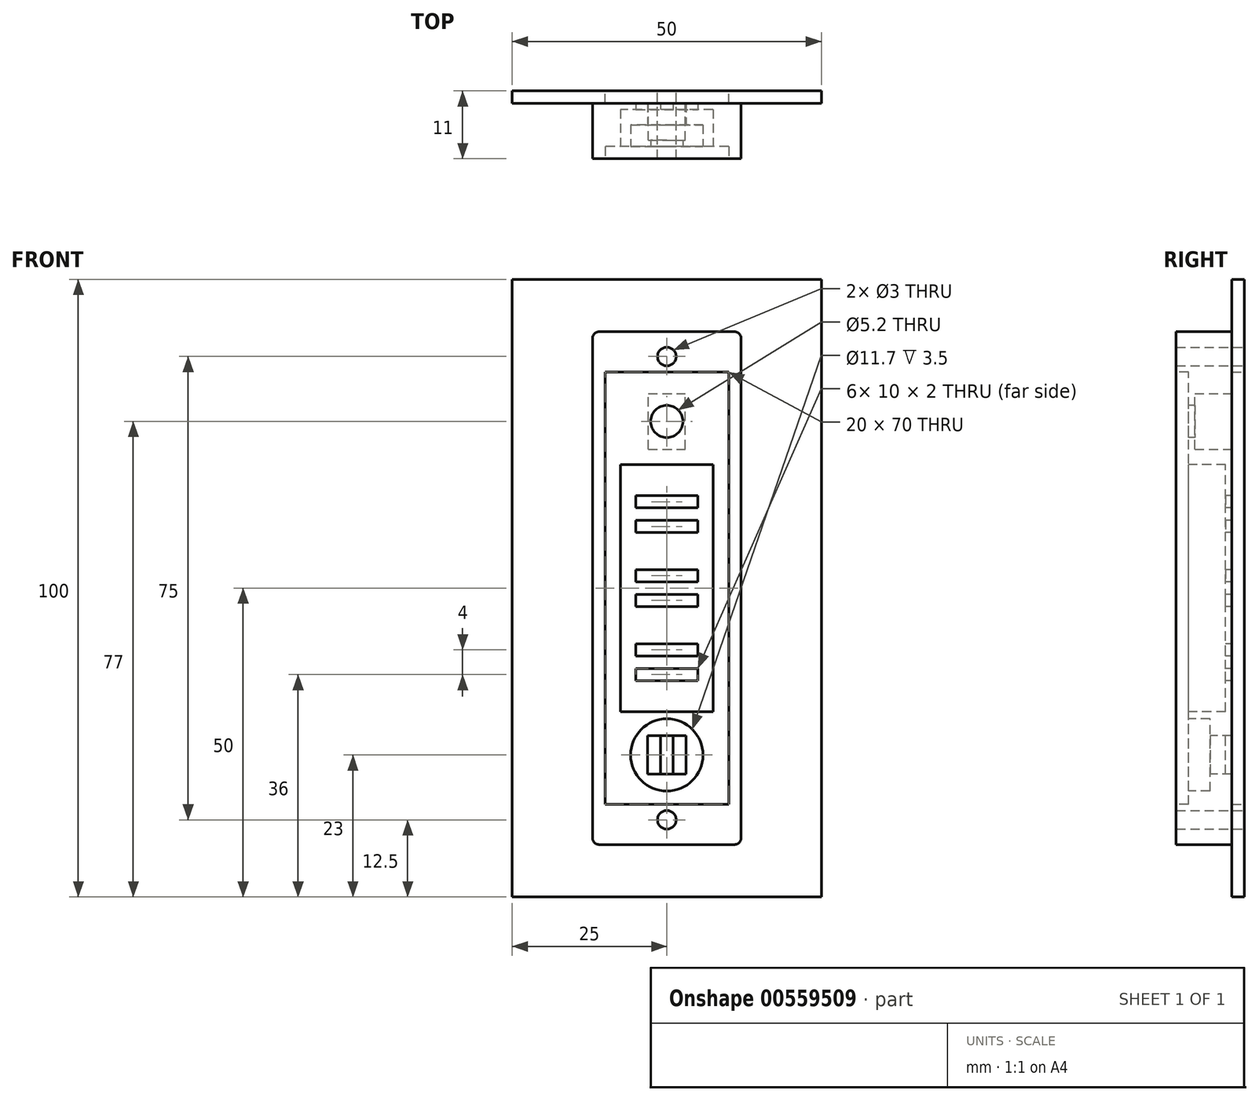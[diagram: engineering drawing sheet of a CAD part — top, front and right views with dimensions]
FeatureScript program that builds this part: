
annotation { "Feature Type Name" : "Feature", "Feature Type Description" : "" }
export const myFeature = defineFeature(function(context is Context, id is Id, definition is map)
    precondition{}
    {
        {
            var Q0;
            Q0=qCreatedBy(makeId("Front.planeOp"),FACE);
            var sketch = newSketch(context, id + "F0", { "sketchPlane" : qUnion([Q0])});
            skLineSegment(sketch, "E0.bottom", {"start": v(25, -50) * mm, "end": v(-25, -50) * mm});
            skLineSegment(sketch, "E0.top", {"start": v(25, 50) * mm, "end": v(-25, 50) * mm});
            skLineSegment(sketch, "E0.left", {"start": v(25, -50) * mm, "end": v(25, 50) * mm});
            skLineSegment(sketch, "E0.right", {"start": v(-25, -50) * mm, "end": v(-25, 50) * mm});
            skPoint(sketch, "E0.middle", {"position": v(0, 0) * mm});
            skLineSegment(sketch, "E1.bottom", {"start": v(10, -35) * mm, "end": v(-10, -35) * mm});
            skLineSegment(sketch, "E1.top", {"start": v(10, 35) * mm, "end": v(-10, 35) * mm});
            skLineSegment(sketch, "E1.left", {"start": v(10, -35) * mm, "end": v(10, 35) * mm});
            skLineSegment(sketch, "E1.right", {"start": v(-10, -35) * mm, "end": v(-10, 35) * mm});
            skCircle(sketch, "E2", {"center": v(0, 37.5) * mm, "radius": 1.5 * mm});
            skCircle(sketch, "E3", {"center": v(0, -37.5) * mm, "radius": 1.5 * mm});
            skSolve(sketch);
        }
        {
            var Q0;
            Q0=qSketchRegion(id+"F0",true);
            extrude(context, id + "F1", {"entities" : qUnion([Q0]), "depth" : 2 * mm});
        }
        {
            var Q0;
            Q0=makeQuery(id+"F1.opExtrude","CAP_FACE",FACE,{"disambiguationData":[OSD([sQuery(id+"F0.wireOp",EDGE,"E0.bottom"),sQuery(id+"F0.wireOp",EDGE,"E0.top"),sQuery(id+"F0.wireOp",EDGE,"E0.left"),sQuery(id+"F0.wireOp",EDGE,"E0.right"),sQuery(id+"F0.wireOp",EDGE,"E1.bottom"),sQuery(id+"F0.wireOp",EDGE,"E1.top"),sQuery(id+"F0.wireOp",EDGE,"E1.left"),sQuery(id+"F0.wireOp",EDGE,"E1.right"),sQuery(id+"F0.wireOp",EDGE,"E2"),sQuery(id+"F0.wireOp",EDGE,"E3")])],"isStart":false});
            var sketch = newSketch(context, id + "F2", { "sketchPlane" : qUnion([Q0])});
            skLineSegment(sketch, "E4.bottom", {"start": v(12, -41.5) * mm, "end": v(-12, -41.5) * mm});
            skLineSegment(sketch, "E4.top", {"start": v(12, 41.5) * mm, "end": v(-12, 41.5) * mm});
            skLineSegment(sketch, "E4.left", {"start": v(12, -41.5) * mm, "end": v(12, 41.5) * mm});
            skLineSegment(sketch, "E4.right", {"start": v(-12, -41.5) * mm, "end": v(-12, 41.5) * mm});
            skPoint(sketch, "E4.middle", {"position": v(0, 0) * mm});
            skCircle(sketch, "E5", {"center": v(0, 37.5) * mm, "radius": 1.5 * mm});
            skCircle(sketch, "E6", {"center": v(0, -37.5) * mm, "radius": 1.5 * mm});
            skSolve(sketch);
        }
        {
            var Q0;
            Q0=qSketchRegion(id+"F2",true);
            extrude(context, id + "F3", {"entities" : qUnion([Q0]), "depth" : 9 * mm});
        }
        {
            var Q0;
            Q0=makeQuery(id+"F3.opExtrude","CAP_FACE",FACE,{"disambiguationData":[OSD([sQuery(id+"F2.wireOp",EDGE,"E4.bottom"),sQuery(id+"F2.wireOp",EDGE,"E4.top"),sQuery(id+"F2.wireOp",EDGE,"E4.left"),sQuery(id+"F2.wireOp",EDGE,"E4.right")])],"isStart":false});
            var sketch = newSketch(context, id + "F4", { "sketchPlane" : qUnion([Q0])});
            skLineSegment(sketch, "E7.bottom", {"start": v(10, -35) * mm, "end": v(-10, -35) * mm});
            skLineSegment(sketch, "E7.top", {"start": v(10, 35) * mm, "end": v(-10, 35) * mm});
            skLineSegment(sketch, "E7.left", {"start": v(10, -35) * mm, "end": v(10, 35) * mm});
            skLineSegment(sketch, "E7.right", {"start": v(-10, -35) * mm, "end": v(-10, 35) * mm});
            skPoint(sketch, "E7.middle", {"position": v(0, 0) * mm});
            skSolve(sketch);
        }
        {
            var Q0;
            Q0=qSketchRegion(id+"F4",true);
            extrude(context, id + "F5", {"entities" : qUnion([Q0]), "operationType" : NewBodyOperationType.REMOVE, "oppositeDirection" : true, "depth" : 14 * mm});
        }
        {
            var Q0;
            Q0=makeQuery(id+"F1.opExtrude","CAP_FACE",FACE,{"disambiguationData":[OSD([sQuery(id+"F0.wireOp",EDGE,"E0.bottom"),sQuery(id+"F0.wireOp",EDGE,"E0.top"),sQuery(id+"F0.wireOp",EDGE,"E0.left"),sQuery(id+"F0.wireOp",EDGE,"E0.right"),sQuery(id+"F0.wireOp",EDGE,"E1.bottom"),sQuery(id+"F0.wireOp",EDGE,"E1.top"),sQuery(id+"F0.wireOp",EDGE,"E1.left"),sQuery(id+"F0.wireOp",EDGE,"E1.right"),sQuery(id+"F0.wireOp",EDGE,"E2"),sQuery(id+"F0.wireOp",EDGE,"E3")])],"isStart":false});
            cPlane(context, id + "F6", {"entities" : qUnion([Q0]), "cplaneType" : CPlaneType.OFFSET, "offset" : 0 * mm, "width" : 150 * mm, "height" : 150 * mm});
        }
        {
            var Q0;
            Q0=qCreatedBy(id+"F6.planeOp",FACE);
            var sketch = newSketch(context, id + "F7", { "sketchPlane" : qUnion([Q0])});
            skLineSegment(sketch, "E8.bottom", {"start": v(10, -35) * mm, "end": v(-10, -35) * mm});
            skLineSegment(sketch, "E8.top", {"start": v(10, 35) * mm, "end": v(-10, 35) * mm});
            skLineSegment(sketch, "E8.left", {"start": v(10, -35) * mm, "end": v(10, 35) * mm});
            skLineSegment(sketch, "E8.right", {"start": v(-10, -35) * mm, "end": v(-10, 35) * mm});
            skPoint(sketch, "E8.middle", {"position": v(0, 0) * mm});
            skSolve(sketch);
        }
        {
            var Q0;
            Q0=qSketchRegion(id+"F7",true);
            extrude(context, id + "F8", {"entities" : qUnion([Q0]), "operationType" : NewBodyOperationType.ADD, "depth" : 7 * mm});
        }
        {
            var Q0;
            Q0=makeQuery(id+"F8.opExtrude","CAP_FACE",FACE,{"disambiguationData":[OSD([sQuery(id+"F7.wireOp",EDGE,"E8.bottom"),sQuery(id+"F7.wireOp",EDGE,"E8.top"),sQuery(id+"F7.wireOp",EDGE,"E8.left"),sQuery(id+"F7.wireOp",EDGE,"E8.right")])],"isStart":false});
            var sketch = newSketch(context, id + "F9", { "sketchPlane" : qUnion([Q0])});
            skCircle(sketch, "E9", {"center": v(0, 27) * mm, "radius": 2.6 * mm});
            skLineSegment(sketch, "E10.bottom", {"start": v(2.5, 23) * mm, "end": v(-2.5, 23) * mm, "construction": true});
            skLineSegment(sketch, "E10.top", {"start": v(2.5, 31) * mm, "end": v(-2.5, 31) * mm, "construction": true});
            skLineSegment(sketch, "E10.left", {"start": v(2.5, 23) * mm, "end": v(2.5, 31) * mm, "construction": true});
            skLineSegment(sketch, "E10.right", {"start": v(-2.5, 23) * mm, "end": v(-2.5, 31) * mm, "construction": true});
            skCircle(sketch, "E11", {"center": v(-7.5, 32.5) * mm, "radius": 1 * mm, "construction": true});
            skCircle(sketch, "E12", {"center": v(7.5, 32.5) * mm, "radius": 1 * mm, "construction": true});
            skCircle(sketch, "E13", {"center": v(-7.5, -32.5) * mm, "radius": 1 * mm, "construction": true});
            skCircle(sketch, "E14", {"center": v(7.5, -32.5) * mm, "radius": 1 * mm, "construction": true});
            skSolve(sketch);
        }
        {
            var Q0;
            Q0=qSketchRegion(id+"F9",true);
            extrude(context, id + "F10", {"entities" : qUnion([Q0]), "operationType" : NewBodyOperationType.REMOVE, "oppositeDirection" : true, "depth" : 5 * mm});
        }
        {
            var Q0;
            Q0=makeQuery(id+"F8.opExtrude","CAP_FACE",FACE,{"disambiguationData":[OSD([sQuery(id+"F7.wireOp",EDGE,"E8.bottom"),sQuery(id+"F7.wireOp",EDGE,"E8.top"),sQuery(id+"F7.wireOp",EDGE,"E8.left"),sQuery(id+"F7.wireOp",EDGE,"E8.right")])],"isStart":true});
            var sketch = newSketch(context, id + "F11", { "sketchPlane" : qUnion([Q0])});
            skLineSegment(sketch, "E15.bottom", {"start": v(3, 22.5) * mm, "end": v(-3, 22.5) * mm});
            skLineSegment(sketch, "E15.top", {"start": v(3, 31.5) * mm, "end": v(-3, 31.5) * mm});
            skLineSegment(sketch, "E15.left", {"start": v(3, 22.5) * mm, "end": v(3, 31.5) * mm});
            skLineSegment(sketch, "E15.right", {"start": v(-3, 22.5) * mm, "end": v(-3, 31.5) * mm});
            skPoint(sketch, "E15.middle", {"position": v(0, 27) * mm});
            skSolve(sketch);
        }
        {
            var Q0;
            Q0=qSketchRegion(id+"F11",true);
            extrude(context, id + "F12", {"entities" : qUnion([Q0]), "operationType" : NewBodyOperationType.REMOVE, "oppositeDirection" : true, "depth" : 6 * mm});
        }
        {
            var Q0;
            Q0=makeQuery(id+"F8.opExtrude","CAP_FACE",FACE,{"disambiguationData":[OSD([sQuery(id+"F7.wireOp",EDGE,"E8.bottom"),sQuery(id+"F7.wireOp",EDGE,"E8.top"),sQuery(id+"F7.wireOp",EDGE,"E8.left"),sQuery(id+"F7.wireOp",EDGE,"E8.right")])],"isStart":false});
            var sketch = newSketch(context, id + "F13", { "sketchPlane" : qUnion([Q0])});
            skLineSegment(sketch, "E16.bottom", {"start": v(5, 13) * mm, "end": v(-5, 13) * mm});
            skLineSegment(sketch, "E16.top", {"start": v(5, 15) * mm, "end": v(-5, 15) * mm});
            skLineSegment(sketch, "E16.left", {"start": v(5, 13) * mm, "end": v(5, 15) * mm});
            skLineSegment(sketch, "E16.right", {"start": v(-5, 13) * mm, "end": v(-5, 15) * mm});
            skPoint(sketch, "E16.middle", {"position": v(0, 14) * mm});
            skLineSegment(sketch, "E17.bottom", {"start": v(5, 9) * mm, "end": v(-5, 9) * mm});
            skLineSegment(sketch, "E17.top", {"start": v(5, 11) * mm, "end": v(-5, 11) * mm});
            skLineSegment(sketch, "E17.left", {"start": v(5, 9) * mm, "end": v(5, 11) * mm});
            skLineSegment(sketch, "E17.right", {"start": v(-5, 9) * mm, "end": v(-5, 11) * mm});
            skPoint(sketch, "E17.middle", {"position": v(0, 10) * mm});
            skLineSegment(sketch, "E18.bottom", {"start": v(5, 1) * mm, "end": v(-5, 1) * mm});
            skLineSegment(sketch, "E18.top", {"start": v(5, 3) * mm, "end": v(-5, 3) * mm});
            skLineSegment(sketch, "E18.left", {"start": v(5, 1) * mm, "end": v(5, 3) * mm});
            skLineSegment(sketch, "E18.right", {"start": v(-5, 1) * mm, "end": v(-5, 3) * mm});
            skPoint(sketch, "E18.middle", {"position": v(0, 2) * mm});
            skLineSegment(sketch, "E19.bottom", {"start": v(5, -1) * mm, "end": v(-5, -1) * mm});
            skLineSegment(sketch, "E19.top", {"start": v(5, -3) * mm, "end": v(-5, -3) * mm});
            skLineSegment(sketch, "E19.left", {"start": v(5, -1) * mm, "end": v(5, -3) * mm});
            skLineSegment(sketch, "E19.right", {"start": v(-5, -1) * mm, "end": v(-5, -3) * mm});
            skPoint(sketch, "E19.middle", {"position": v(0, -2) * mm});
            skLineSegment(sketch, "E20.bottom", {"start": v(5, -9) * mm, "end": v(-5, -9) * mm});
            skLineSegment(sketch, "E20.top", {"start": v(5, -11) * mm, "end": v(-5, -11) * mm});
            skLineSegment(sketch, "E20.left", {"start": v(5, -9) * mm, "end": v(5, -11) * mm});
            skLineSegment(sketch, "E20.right", {"start": v(-5, -9) * mm, "end": v(-5, -11) * mm});
            skPoint(sketch, "E20.middle", {"position": v(0, -10) * mm});
            skPoint(sketch, "E20.middle.positionSnap0", {"position": v(0, -3) * mm});
            skPoint(sketch, "E20.centerSnap0", {"position": v(0, -3) * mm});
            skLineSegment(sketch, "E21.bottom", {"start": v(5, -13) * mm, "end": v(-5, -13) * mm});
            skLineSegment(sketch, "E21.top", {"start": v(5, -15) * mm, "end": v(-5, -15) * mm});
            skLineSegment(sketch, "E21.left", {"start": v(5, -13) * mm, "end": v(5, -15) * mm});
            skLineSegment(sketch, "E21.right", {"start": v(-5, -13) * mm, "end": v(-5, -15) * mm});
            skPoint(sketch, "E21.middle", {"position": v(0, -14) * mm});
            skSolve(sketch);
        }
        {
            var Q0;
            Q0=qSketchRegion(id+"F13",true);
            extrude(context, id + "F14", {"entities" : qUnion([Q0]), "operationType" : NewBodyOperationType.REMOVE, "oppositeDirection" : true, "depth" : 10 * mm});
        }
        {
            var Q0;
            Q0=makeQuery(id+"F8.opExtrude","CAP_FACE",FACE,{"disambiguationData":[OSD([sQuery(id+"F7.wireOp",EDGE,"E8.bottom"),sQuery(id+"F7.wireOp",EDGE,"E8.top"),sQuery(id+"F7.wireOp",EDGE,"E8.left"),sQuery(id+"F7.wireOp",EDGE,"E8.right")])],"isStart":false});
            var sketch = newSketch(context, id + "F15", { "sketchPlane" : qUnion([Q0])});
            skLineSegment(sketch, "E22.bottom", {"start": v(7.5, -20) * mm, "end": v(-7.5, -20) * mm});
            skLineSegment(sketch, "E22.top", {"start": v(7.5, 20) * mm, "end": v(-7.5, 20) * mm});
            skLineSegment(sketch, "E22.left", {"start": v(7.5, -20) * mm, "end": v(7.5, 20) * mm});
            skLineSegment(sketch, "E22.right", {"start": v(-7.5, -20) * mm, "end": v(-7.5, 20) * mm});
            skPoint(sketch, "E22.middle", {"position": v(0, 0) * mm});
            skSolve(sketch);
        }
        {
            var Q0;
            Q0=qSketchRegion(id+"F15",true);
            extrude(context, id + "F16", {"entities" : qUnion([Q0]), "operationType" : NewBodyOperationType.REMOVE, "oppositeDirection" : true, "depth" : 6 * mm});
        }
        {
            var Q0;
            Q0=makeQuery(id+"F8.opExtrude","CAP_FACE",FACE,{"disambiguationData":[OSD([sQuery(id+"F7.wireOp",EDGE,"E8.bottom"),sQuery(id+"F7.wireOp",EDGE,"E8.top"),sQuery(id+"F7.wireOp",EDGE,"E8.left"),sQuery(id+"F7.wireOp",EDGE,"E8.right")])],"isStart":false});
            var sketch = newSketch(context, id + "F17", { "sketchPlane" : qUnion([Q0])});
            skLineSegment(sketch, "E23.bottom", {"start": v(3.1, -30.1) * mm, "end": v(-3.1, -30.1) * mm});
            skLineSegment(sketch, "E23.top", {"start": v(3.1, -23.9) * mm, "end": v(-3.1, -23.9) * mm});
            skLineSegment(sketch, "E23.left", {"start": v(3.1, -30.1) * mm, "end": v(3.1, -23.9) * mm});
            skLineSegment(sketch, "E23.right", {"start": v(-3.1, -30.1) * mm, "end": v(-3.1, -23.9) * mm});
            skPoint(sketch, "E23.middle", {"position": v(0, -27) * mm});
            skSolve(sketch);
        }
        {
            var Q0;
            Q0=qSketchRegion(id+"F17",true);
            extrude(context, id + "F18", {"entities" : qUnion([Q0]), "operationType" : NewBodyOperationType.REMOVE, "oppositeDirection" : true, "depth" : 6 * mm});
        }
        {
            var Q0;
            Q0=makeQuery(id+"F18.boolean.opBoolean","COPY",FACE,{"derivedFrom":makeQuery(id+"F18.opExtrude","CAP_FACE",FACE,{"disambiguationData":[OSD([sQuery(id+"F17.wireOp",EDGE,"E23.bottom"),sQuery(id+"F17.wireOp",EDGE,"E23.top"),sQuery(id+"F17.wireOp",EDGE,"E23.left"),sQuery(id+"F17.wireOp",EDGE,"E23.right")])],"isStart":false})});
            var sketch = newSketch(context, id + "F19", { "sketchPlane" : qUnion([Q0])});
            skLineSegment(sketch, "E24.bottom", {"start": v(-1, -30.1) * mm, "end": v(-3.1, -30.1) * mm});
            skLineSegment(sketch, "E24.top", {"start": v(-1, -23.9) * mm, "end": v(-3.1, -23.9) * mm});
            skLineSegment(sketch, "E24.left", {"start": v(-1, -30.1) * mm, "end": v(-1, -23.9) * mm});
            skLineSegment(sketch, "E24.right", {"start": v(-3.1, -30.1) * mm, "end": v(-3.1, -23.9) * mm});
            skPoint(sketch, "E24.middle", {"position": v(-2.05, -27) * mm});
            skPoint(sketch, "E24.middle.positionSnap0", {"position": v(3.1, -27) * mm});
            skPoint(sketch, "E24.centerSnap0", {"position": v(3.1, -27) * mm});
            skLineSegment(sketch, "E25.bottom", {"start": v(3.1, -30.1) * mm, "end": v(1, -30.1) * mm});
            skLineSegment(sketch, "E25.top", {"start": v(3.1, -23.9) * mm, "end": v(1, -23.9) * mm});
            skLineSegment(sketch, "E25.left", {"start": v(3.1, -30.1) * mm, "end": v(3.1, -23.9) * mm});
            skLineSegment(sketch, "E25.right", {"start": v(1, -30.1) * mm, "end": v(1, -23.9) * mm});
            skPoint(sketch, "E25.middle", {"position": v(2.05, -27) * mm});
            skSolve(sketch);
        }
        {
            var Q0;
            Q0=qSketchRegion(id+"F19",true);
            extrude(context, id + "F20", {"entities" : qUnion([Q0]), "operationType" : NewBodyOperationType.REMOVE, "oppositeDirection" : true, "depth" : 1 * mm});
        }
        {
            var Q0;
            Q0=makeQuery(id+"F8.opExtrude","CAP_FACE",FACE,{"disambiguationData":[OSD([sQuery(id+"F7.wireOp",EDGE,"E8.bottom"),sQuery(id+"F7.wireOp",EDGE,"E8.top"),sQuery(id+"F7.wireOp",EDGE,"E8.left"),sQuery(id+"F7.wireOp",EDGE,"E8.right")])],"isStart":false});
            var sketch = newSketch(context, id + "F21", { "sketchPlane" : qUnion([Q0])});
            skCircle(sketch, "E26", {"center": v(0, -27) * mm, "radius": 5.85 * mm});
            skPoint(sketch, "E26.centerSnap0", {"position": v(3.1, -27) * mm});
            skPoint(sketch, "E26.centerSnap1", {"position": v(0, -23.9) * mm});
            skSolve(sketch);
        }
        {
            var Q0;
            Q0=qSketchRegion(id+"F21",true);
            extrude(context, id + "F22", {"entities" : qUnion([Q0]), "operationType" : NewBodyOperationType.REMOVE, "oppositeDirection" : true, "depth" : 3.5 * mm});
        }
        {
            var Q0;
            Q0=makeQuery(id+"F3.opExtrude","SWEPT_EDGE",EDGE,{"disambiguationData":[OSD([sQuery(id+"F2.wireOp",EDGE,"E4.bottom"),sQuery(id+"F2.wireOp",EDGE,"E4.right")])]});
            var Q1;
            Q1=makeQuery(id+"F3.opExtrude","SWEPT_EDGE",EDGE,{"disambiguationData":[OSD([sQuery(id+"F2.wireOp",EDGE,"E4.bottom"),sQuery(id+"F2.wireOp",EDGE,"E4.left")])]});
            var Q2;
            Q2=makeQuery(id+"F3.opExtrude","SWEPT_EDGE",EDGE,{"disambiguationData":[OSD([sQuery(id+"F2.wireOp",EDGE,"E4.top"),sQuery(id+"F2.wireOp",EDGE,"E4.right")])]});
            var Q3;
            Q3=makeQuery(id+"F3.opExtrude","SWEPT_EDGE",EDGE,{"disambiguationData":[OSD([sQuery(id+"F2.wireOp",EDGE,"E4.top"),sQuery(id+"F2.wireOp",EDGE,"E4.left")])]});
            fillet(context, id + "F23", {"entities" : qUnion([Q0, Q1, Q2, Q3]), "radius" : 1 * mm, "tangentPropagation" : true, "allowEdgeOverflow" : false});
        }
    });
